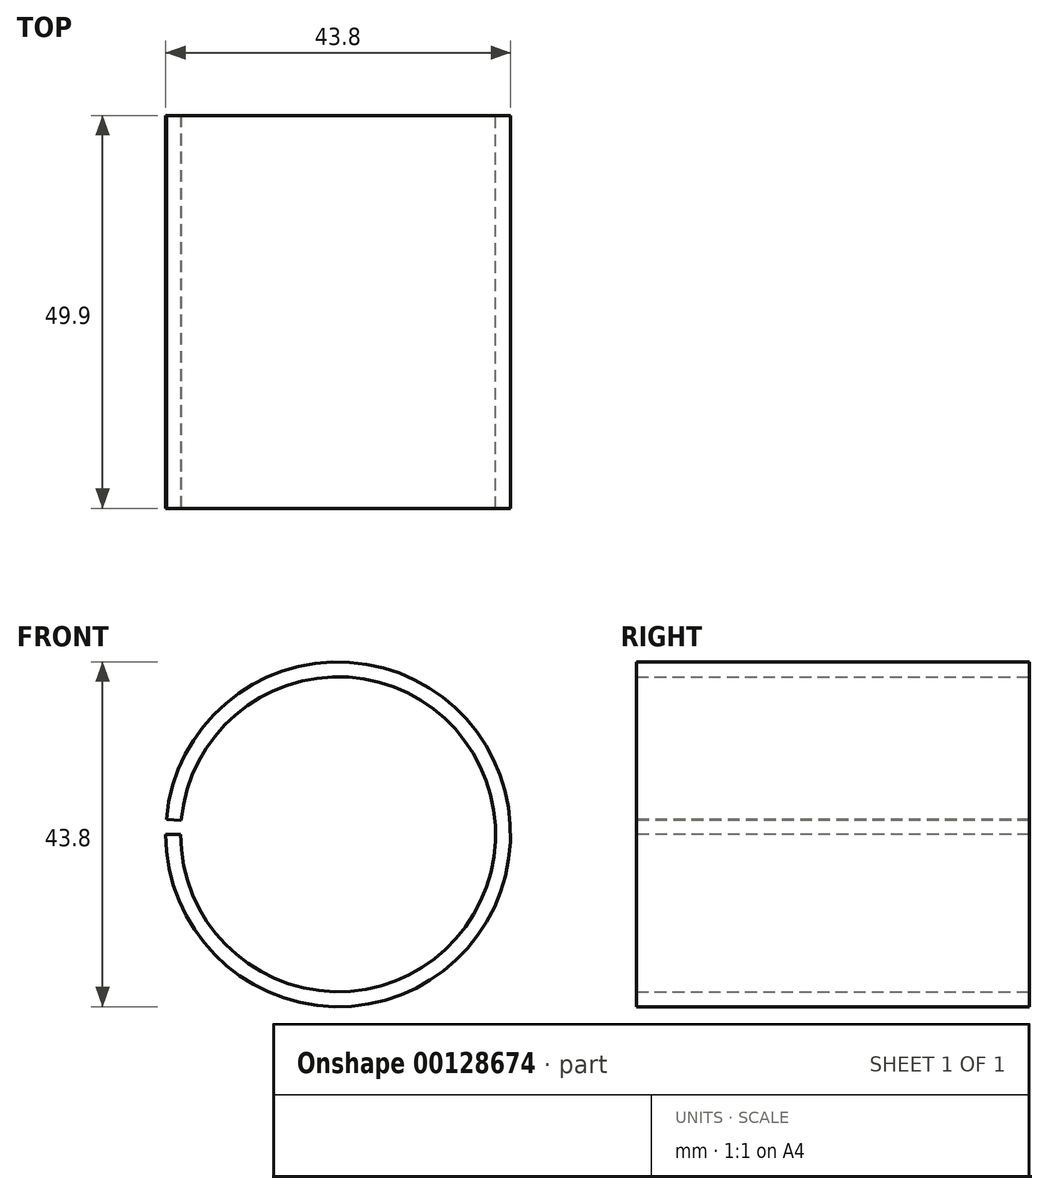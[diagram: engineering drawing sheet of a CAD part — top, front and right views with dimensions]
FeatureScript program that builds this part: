
annotation { "Feature Type Name" : "Feature", "Feature Type Description" : "" }
export const myFeature = defineFeature(function(context is Context, id is Id, definition is map)
    precondition{}
    {
        {
            var Q0;
            Q0=qCreatedBy(makeId("Top.planeOp"),FACE);
            var sketch = newSketch(context, id + "F0", { "sketchPlane" : qUnion([Q0])});
            skLineSegment(sketch, "E0", {"start": v(0, 0) * mm, "end": v(0, -38.08) * mm, "construction": true});
            skLineSegment(sketch, "E1.bottom", {"start": v(-21.9, 0) * mm, "end": v(-20, 0) * mm});
            skLineSegment(sketch, "E1.top", {"start": v(-21.9, -49.9) * mm, "end": v(-20, -49.9) * mm});
            skLineSegment(sketch, "E1.left", {"start": v(-21.9, 0) * mm, "end": v(-21.9, -49.9) * mm});
            skLineSegment(sketch, "E1.right", {"start": v(-20, 0) * mm, "end": v(-20, -49.9) * mm});
            skSolve(sketch);
        }
        {
            var Q0;
            Q0=makeQuery(id+"F0.imprint","IMPRINT",FACE,{"disambiguationData":[TD([[makeQuery(id+"F0.imprint","IMPRINT",EDGE,{"derivedFrom":sQuery(id+"F0.wireOp",EDGE,"E1.bottom")}),-1.0]])]});
            var Q1;
            Q1=sQuery(id+"F0.wireOp",EDGE,"E0");
            revolve(context, id + "F1", {"entities" : qUnion([Q0]), "axis" : qUnion([Q1]), "revolveType" : RevolveType.ONE_DIRECTION, "angle" : 355 * degree});
        }
    });
